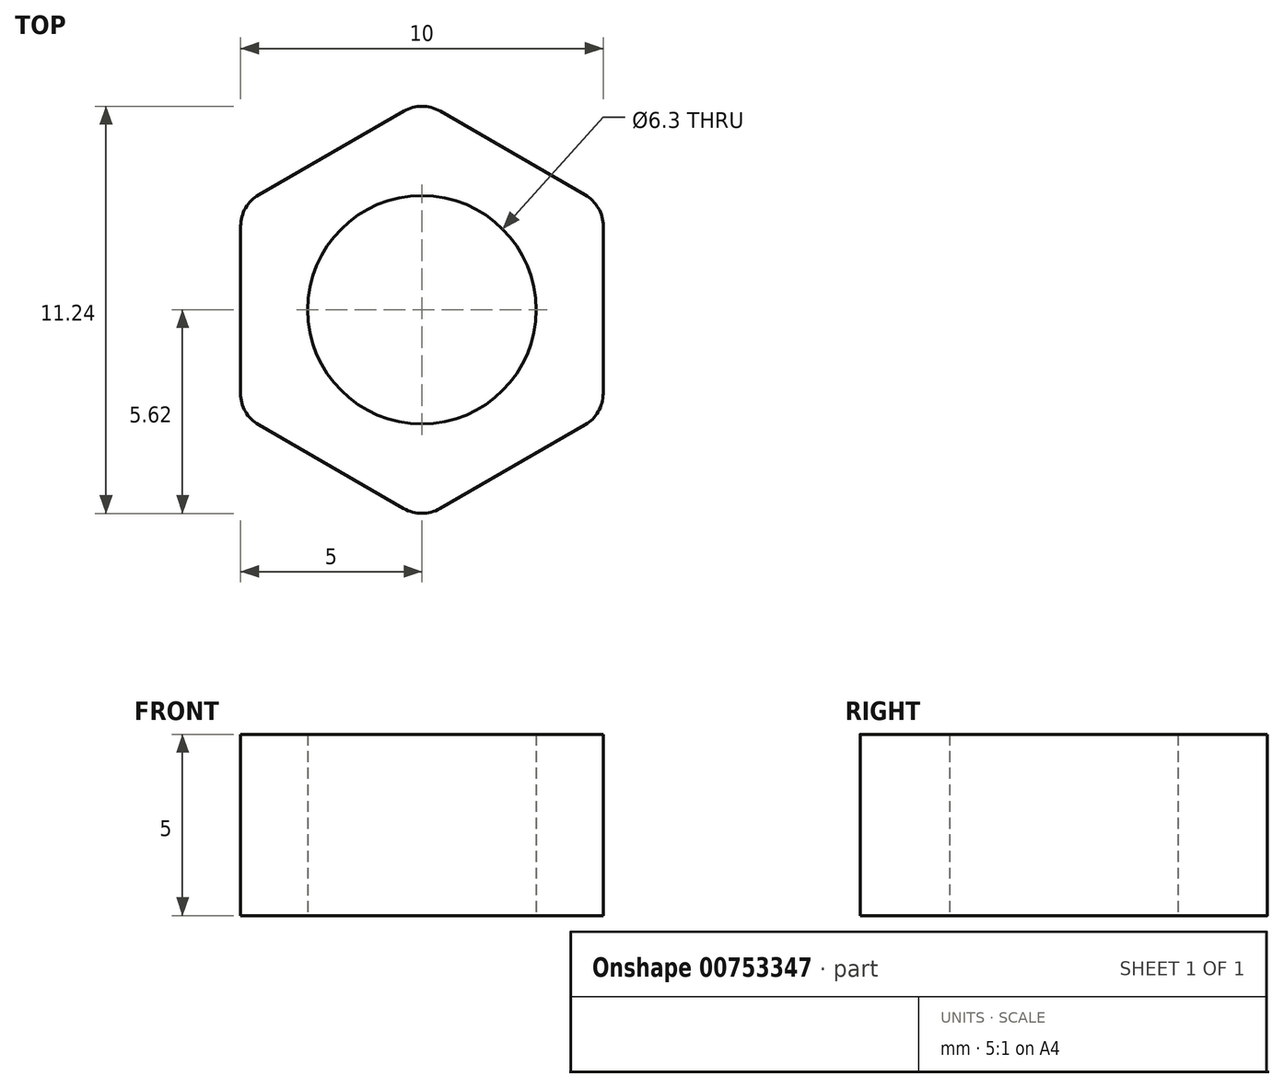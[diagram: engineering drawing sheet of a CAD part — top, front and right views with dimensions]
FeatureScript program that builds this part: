
annotation { "Feature Type Name" : "Feature", "Feature Type Description" : "" }
export const myFeature = defineFeature(function(context is Context, id is Id, definition is map)
    precondition{}
    {
        {
            var Q0;
            Q0=qCreatedBy(makeId("Top.planeOp"),FACE);
            var sketch = newSketch(context, id + "F0", { "sketchPlane" : qUnion([Q0])});
            skCircle(sketch, "E0.cCircle", {"center": v(0, 0) * mm, "radius": 5 * mm, "construction": true});
            skLineSegment(sketch, "E0.0", {"start": v(0, 5.77) * mm, "end": v(5, 2.88) * mm});
            skLineSegment(sketch, "E0.1", {"start": v(5, 2.88) * mm, "end": v(5, -2.89) * mm});
            skLineSegment(sketch, "E0.2", {"start": v(5, -2.89) * mm, "end": v(0, -5.77) * mm});
            skLineSegment(sketch, "E0.3", {"start": v(0, -5.77) * mm, "end": v(-5, -2.88) * mm});
            skLineSegment(sketch, "E0.4", {"start": v(-5, -2.88) * mm, "end": v(-5, 2.89) * mm});
            skLineSegment(sketch, "E0.5", {"start": v(-5, 2.89) * mm, "end": v(0, 5.77) * mm});
            skPoint(sketch, "E0.0.midPoint", {"position": v(2.5, 4.33) * mm});
            skSolve(sketch);
        }
        {
            var Q0;
            Q0=makeQuery(id+"F0.imprint","IMPRINT",FACE,{"disambiguationData":[TD([[makeQuery(id+"F0.imprint","IMPRINT",EDGE,{"derivedFrom":sQuery(id+"F0.wireOp",EDGE,"E0.0")}),-1.0]])]});
            extrude(context, id + "F1", {"entities" : qUnion([Q0]), "depth" : 5 * mm, "offsetDistance" : 25 * mm});
        }
        {
            var Q0;
            Q0=sQuery(id+"F0.wireOp",VERTEX,"E0.cCircle.center");
            var Q1;
            Q1=makeQuery(id+"F1.opExtrude","SWEPT_BODY",BODY,{"disambiguationData":[OSD([sQuery(id+"F0.wireOp",EDGE,"E0.0"),sQuery(id+"F0.wireOp",EDGE,"E0.1"),sQuery(id+"F0.wireOp",EDGE,"E0.2"),sQuery(id+"F0.wireOp",EDGE,"E0.3"),sQuery(id+"F0.wireOp",EDGE,"E0.4"),sQuery(id+"F0.wireOp",EDGE,"E0.5")])]});
            hole(context, id + "F2", {"style" : HoleStyle.SIMPLE, "endStyle" : HoleEndStyle.THROUGH, "oppositeDirection" : true, "standardTappedOrClearance" : lookupTablePath({ "fit" : "Close", "standard" : "ISO", "size" : "M6", "type" : "Clearance" }), "standardBlindInLast" : lookupTablePath({ "fit" : "Close", "standard" : "ISO", "size" : "M6", "type" : "Clearance" }), "holeDiameter" : 6.3 * mm, "majorDiameter" : 5 * mm, "isTappedThrough" : true, "tappedDepth" : 12 * mm, "tapClearance" : 3, "locations" : qUnion([Q0]), "scope" : qUnion([Q1])});
        }
        {
            var Q0;
            Q0=makeQuery(id+"F1.opExtrude","SWEPT_EDGE",EDGE,{"disambiguationData":[OSD([sQuery(id+"F0.wireOp",EDGE,"E0.2"),sQuery(id+"F0.wireOp",EDGE,"E0.3")])]});
            var Q1;
            Q1=makeQuery(id+"F1.opExtrude","SWEPT_EDGE",EDGE,{"disambiguationData":[OSD([sQuery(id+"F0.wireOp",EDGE,"E0.1"),sQuery(id+"F0.wireOp",EDGE,"E0.2")])]});
            var Q2;
            Q2=makeQuery(id+"F1.opExtrude","SWEPT_EDGE",EDGE,{"disambiguationData":[OSD([sQuery(id+"F0.wireOp",EDGE,"E0.0"),sQuery(id+"F0.wireOp",EDGE,"E0.1")])]});
            var Q3;
            Q3=makeQuery(id+"F1.opExtrude","SWEPT_EDGE",EDGE,{"disambiguationData":[OSD([sQuery(id+"F0.wireOp",EDGE,"E0.0"),sQuery(id+"F0.wireOp",EDGE,"E0.5")])]});
            var Q4;
            Q4=makeQuery(id+"F1.opExtrude","SWEPT_EDGE",EDGE,{"disambiguationData":[OSD([sQuery(id+"F0.wireOp",EDGE,"E0.4"),sQuery(id+"F0.wireOp",EDGE,"E0.5")])]});
            var Q5;
            Q5=makeQuery(id+"F1.opExtrude","SWEPT_EDGE",EDGE,{"disambiguationData":[OSD([sQuery(id+"F0.wireOp",EDGE,"E0.3"),sQuery(id+"F0.wireOp",EDGE,"E0.4")])]});
            fillet(context, id + "F3", {"entities" : qUnion([Q0, Q1, Q2, Q3, Q4, Q5]), "radius" : 1 * mm, "allowEdgeOverflow" : false});
        }
    });
